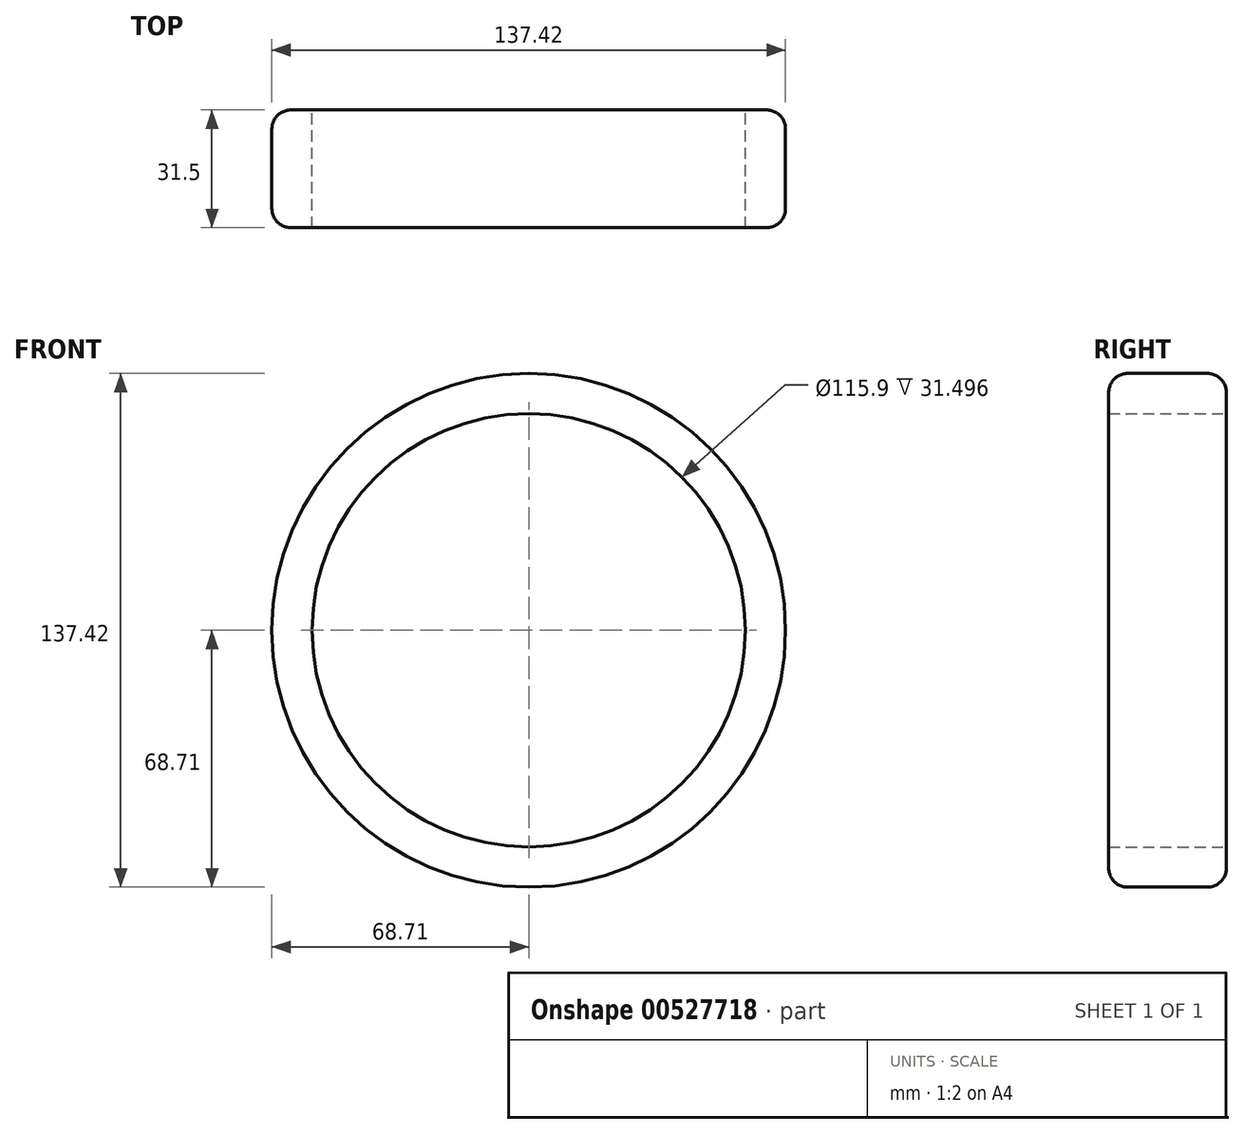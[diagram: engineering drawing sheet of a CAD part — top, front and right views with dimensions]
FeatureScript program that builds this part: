
annotation { "Feature Type Name" : "Feature", "Feature Type Description" : "" }
export const myFeature = defineFeature(function(context is Context, id is Id, definition is map)
    precondition{}
    {
        {
            var Q0;
            Q0=qCreatedBy(makeId("Front.planeOp"),FACE);
            var sketch = newSketch(context, id + "F0", { "sketchPlane" : qUnion([Q0])});
            skCircle(sketch, "E0", {"center": v(0, 0) * mm, "radius": 68.7 * mm});
            skCircle(sketch, "E1", {"center": v(0, 0) * mm, "radius": 57.95 * mm});
            skSolve(sketch);
        }
        {
            var Q0;
            Q0=makeQuery(id+"F0.imprint","IMPRINT",FACE,{"disambiguationData":[TD([[makeQuery(id+"F0.imprint","IMPRINT",EDGE,{"derivedFrom":sQuery(id+"F0.wireOp",EDGE,"E0")}),1.0]])]});
            extrude(context, id + "F1", {"entities" : qUnion([Q0]), "depth" : 31.5 * mm, "offsetDistance" : 25.4 * mm});
        }
        {
            var Q0;
            Q0=makeQuery(id+"F1.opExtrude","CAP_EDGE",EDGE,{"disambiguationData":[OSD([sQuery(id+"F0.wireOp",EDGE,"E0")])],"isStart":false});
            fillet(context, id + "F2", {"entities" : qUnion([Q0]), "radius" : 5.08 * mm, "tangentPropagation" : true, "allowEdgeOverflow" : false});
        }
        {
            var Q0;
            Q0=makeQuery(id+"F1.opExtrude","CAP_EDGE",EDGE,{"disambiguationData":[OSD([sQuery(id+"F0.wireOp",EDGE,"E0")])],"isStart":true});
            fillet(context, id + "F3", {"entities" : qUnion([Q0]), "radius" : 5.08 * mm, "tangentPropagation" : true, "allowEdgeOverflow" : false});
        }
    });
